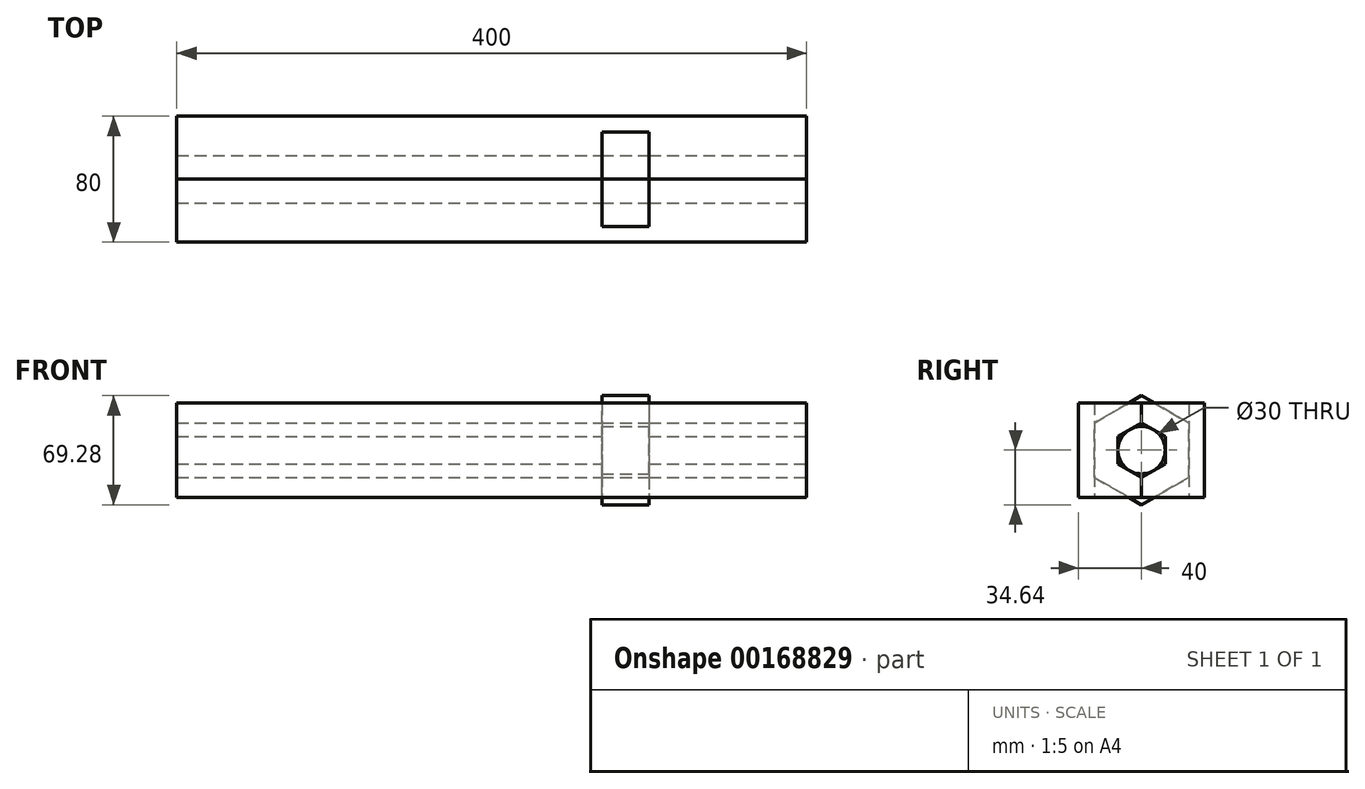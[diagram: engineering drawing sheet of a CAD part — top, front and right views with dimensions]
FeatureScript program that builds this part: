
annotation { "Feature Type Name" : "Feature", "Feature Type Description" : "" }
export const myFeature = defineFeature(function(context is Context, id is Id, definition is map)
    precondition{}
    {
        {
            assignVariable(context, id + "F0", {"name" : "t", "anyValue" : 40 * mm});
        }
        {
            var Q0;
            Q0=qCreatedBy(makeId("Front.planeOp"),FACE);
            var sketch = newSketch(context, id + "F1", { "sketchPlane" : qUnion([Q0])});
            skLineSegment(sketch, "E0.bottom", {"start": v(200, -30) * mm, "end": v(-200, -30) * mm});
            skLineSegment(sketch, "E0.top", {"start": v(200, 30) * mm, "end": v(-200, 30) * mm});
            skLineSegment(sketch, "E0.left", {"start": v(200, -30) * mm, "end": v(200, 30) * mm});
            skLineSegment(sketch, "E0.right", {"start": v(-200, -30) * mm, "end": v(-200, 30) * mm});
            skPoint(sketch, "E0.middle", {"position": v(0, 0) * mm});
            skSolve(sketch);
        }
        {
            var Q0;
            Q0=qSketchRegion(id+"F1",true);
            extrude(context, id + "F2", {"entities" : qUnion([Q0]), "depth" : getVariable(context, 't')});
        }
        {
            var Q0;
            Q0=makeQuery(id+"F2.opExtrude","SWEPT_FACE",FACE,{"disambiguationData":[OSD([sQuery(id+"F1.wireOp",EDGE,"E0.left")])]});
            var sketch = newSketch(context, id + "F3", { "sketchPlane" : qUnion([Q0])});
            skCircle(sketch, "E1", {"center": v(0, 0) * mm, "radius": 15 * mm, "construction": true});
            skLineSegment(sketch, "E2.0", {"start": v(-15, 8.66) * mm, "end": v(0, 17.32) * mm});
            skLineSegment(sketch, "E2.1", {"start": v(0, 17.32) * mm, "end": v(15, 8.66) * mm});
            skLineSegment(sketch, "E2.2", {"start": v(15, 8.66) * mm, "end": v(15, -8.66) * mm});
            skLineSegment(sketch, "E2.3", {"start": v(15, -8.66) * mm, "end": v(0, -17.32) * mm});
            skLineSegment(sketch, "E2.4", {"start": v(0, -17.32) * mm, "end": v(-15, -8.66) * mm});
            skLineSegment(sketch, "E2.5", {"start": v(-15, -8.66) * mm, "end": v(-15, 8.66) * mm});
            skPoint(sketch, "E2.0.midPoint", {"position": v(-7.5, 13) * mm});
            skSolve(sketch);
        }
        {
            var Q0;
            Q0=qSketchRegion(id+"F3",true);
            extrude(context, id + "F4", {"entities" : qUnion([Q0]), "operationType" : NewBodyOperationType.REMOVE, "endBound" : BoundingType.THROUGH_ALL, "oppositeDirection" : true, "depth" : 25 * mm});
        }
        {
            var Q0;
            {var subQ0=sQuery(id+"F1.wireOp",EDGE,"E0.top");var subQ1=sQuery(id+"F1.wireOp",EDGE,"E0.left");var subQ2=sQuery(id+"F1.wireOp",EDGE,"E0.right");Q0=makeQuery(id+"F4.boolean.opBoolean","SPLIT",FACE,{"disambiguationData":[TD([makeQuery(id+"F2.opExtrude","SWEPT_FACE",FACE,{"disambiguationData":[OSD([subQ0])]})])],"derivedFrom":makeQuery(id+"F2.opExtrude","CAP_FACE",FACE,{"disambiguationData":[OSD([sQuery(id+"F1.wireOp",EDGE,"E0.bottom"),subQ0,subQ1,subQ2])],"isStart":true})});}
            var sketch = newSketch(context, id + "F5", { "sketchPlane" : qUnion([Q0])});
            skLineSegment(sketch, "E3.bottom", {"start": v(-100, 30) * mm, "end": v(-70, 30) * mm});
            skLineSegment(sketch, "E3.top", {"start": v(-100, -30) * mm, "end": v(-70, -30) * mm});
            skLineSegment(sketch, "E3.left", {"start": v(-100, 30) * mm, "end": v(-100, -30) * mm});
            skLineSegment(sketch, "E3.right", {"start": v(-70, 30) * mm, "end": v(-70, -30) * mm});
            skSolve(sketch);
        }
        {
            var Q0;
            Q0 = qSketchRegion(id + "F5", true);
            extrude(context, id + "F6", {"entities" : qUnion([Q0]), "operationType" : NewBodyOperationType.REMOVE, "oppositeDirection" : true, "depth" : 30 * mm});
        }
        {
            var Q0;
            Q0=makeQuery(id+"F6.boolean.opBoolean","COPY",FACE,{"derivedFrom":makeQuery(id+"F6.opExtrude","SWEPT_FACE",FACE,{"disambiguationData":[OSD([sQuery(id+"F5.wireOp",EDGE,"E3.left")])]})});
            var sketch = newSketch(context, id + "F7", { "sketchPlane" : qUnion([Q0])});
            skLineSegment(sketch, "E4.0", {"start": v(0, 17.32) * mm, "end": v(15, 8.66) * mm, "construction": true});
            skLineSegment(sketch, "E5.0", {"start": v(15, 8.66) * mm, "end": v(15, -8.66) * mm, "construction": true});
            skLineSegment(sketch, "E6.0", {"start": v(15, -8.66) * mm, "end": v(0, -17.32) * mm, "construction": true});
            skLineSegment(sketch, "E7.0", {"start": v(30, -17.32) * mm, "end": v(0, -34.64) * mm});
            skLineSegment(sketch, "E7.1", {"start": v(30, 17.32) * mm, "end": v(30, -17.32) * mm});
            skLineSegment(sketch, "E7.2", {"start": v(0, 34.64) * mm, "end": v(30, 17.32) * mm});
            skLineSegment(sketch, "E8", {"start": v(0, 17.32) * mm, "end": v(0, -17.32) * mm, "construction": true});
            skLineSegment(sketch, "E9.MirrorCS", {"start": v(0, 34.64) * mm, "end": v(-30, 17.32) * mm});
            skLineSegment(sketch, "E10.MirrorCS", {"start": v(-30, 17.32) * mm, "end": v(-30, -17.32) * mm});
            skLineSegment(sketch, "E11.MirrorCS", {"start": v(-30, -17.32) * mm, "end": v(0, -34.64) * mm});
            skCircle(sketch, "E12", {"center": v(0, 0) * mm, "radius": 15 * mm});
            skSolve(sketch);
        }
        {
            var Q0;
            Q0 = qSketchRegion(id + "F7", true);
            var Q1;
            Q1=makeQuery(id+"F6.boolean.opBoolean","COPY",FACE,{"derivedFrom":makeQuery(id+"F6.opExtrude","SWEPT_FACE",FACE,{"disambiguationData":[OSD([sQuery(id+"F5.wireOp",EDGE,"E3.right")])]})});
            extrude(context, id + "F8", {"entities" : qUnion([Q0]), "endBound" : BoundingType.UP_TO_SURFACE, "endBoundEntityFace" : qUnion([Q1]), "depth" : 25 * mm});
        }
        {
            var Q0;
            Q0=makeQuery(id+"F2.opExtrude","SWEPT_BODY",BODY,{"disambiguationData":[OSD([sQuery(id+"F1.wireOp",EDGE,"E0.bottom"),sQuery(id+"F1.wireOp",EDGE,"E0.top"),sQuery(id+"F1.wireOp",EDGE,"E0.left"),sQuery(id+"F1.wireOp",EDGE,"E0.right")])]});
            var Q1;
            Q1=qCreatedBy(makeId("Front.planeOp"),FACE);
            mirror(context, id + "F9", {"entities" : qUnion([Q0]), "mirrorPlane" : qUnion([Q1])});
        }
    });
